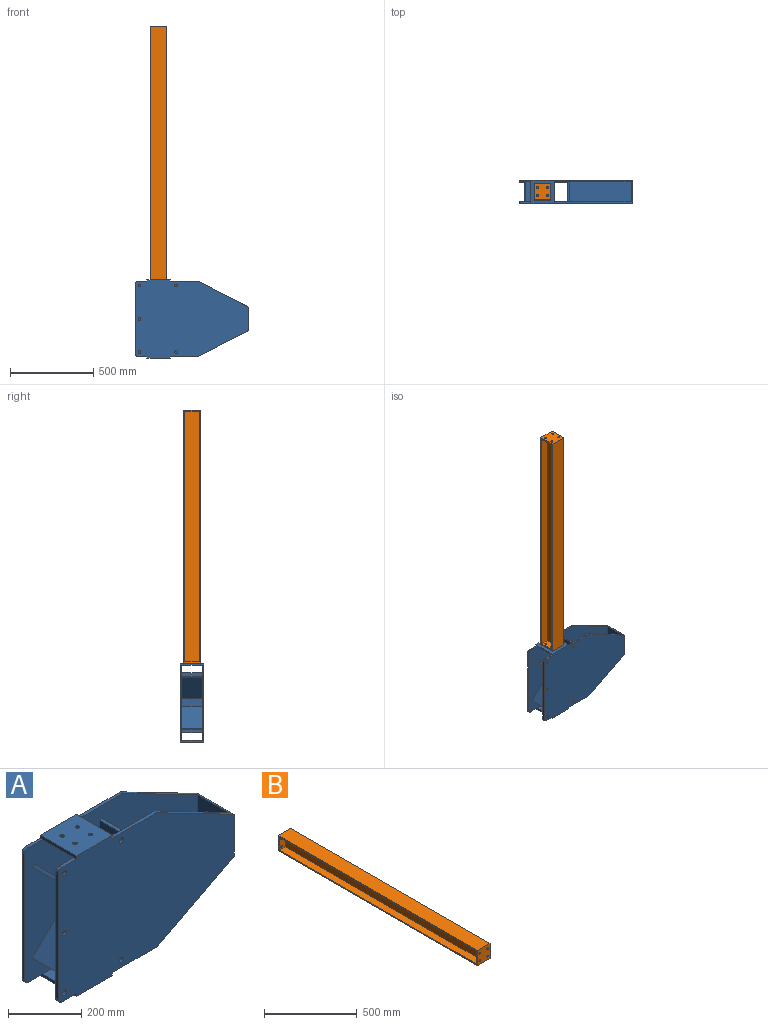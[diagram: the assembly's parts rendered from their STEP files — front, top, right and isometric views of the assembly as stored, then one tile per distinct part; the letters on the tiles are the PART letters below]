
ASSEMBLY  parts=2 mates=1
PART A: 63 faces, bbox 680x140x470 mm
  f0: plane 140x140mm, normal (1,0,0), area 19008.5mm2, adj f11,f12,f19,f41,f59,f60,f61,f62
  f1: plane 120x70.17mm, normal (-1,0,0), area 8124.2mm2, adj f12,f20,f30,f42,f61,f62
  f2: plane 120x70.17mm, normal (-1,0,0), area 8124.2mm2, adj f11,f20,f31,f42,f59,f60
  f3: plane 55x10mm, normal (0,0,-1), area 550mm2, adj f9,f19,f20,f52
  f4: plane 55x10mm, normal (0,0,-1), area 550mm2, adj f40,f41,f42,f52
  f5: plane 55x10mm, normal (0,0,1), area 550mm2, adj f7,f19,f20,f43
  f6: plane 55x10mm, normal (0,0,1), area 550mm2, adj f37,f41,f42,f43
  f7: cylinder r=15mm len=15mm, axis (0,1,0), area 235.6mm2, adj f5,f8,f19,f20
  f8: plane 420x10mm, normal (-1,0,0), area 4200mm2, adj f7,f9,f19,f20
  f9: cylinder r=15mm len=15mm, axis (0,1,0), area 235.6mm2, adj f3,f8,f19,f20
  f10: plane 170x10mm, normal (0,0,-1), area 1700mm2, adj f11,f19,f20,f56
  f11: plane 300x155mm, normal (0.46,0,-0.89), area 8104.2mm2, adj f0,f2,f10,f19,f20,f39,f41,f42
  f12: plane 300x155mm, normal (0.46,0,0.89), area 8104.2mm2, adj f0,f1,f18,f19,f20,f38,f41,f42
  f13: cylinder r=8.5mm len=17mm, axis (0,1,0), area 534.1mm2, adj f19,f20
  f14: cylinder r=8.5mm len=17mm, axis (0,1,0), area 534.1mm2, adj f19,f20
  f15: cylinder r=8.5mm len=17mm, axis (0,1,0), area 534.1mm2, adj f19,f20
  f16: cylinder r=8.5mm len=17mm, axis (0,1,0), area 534.1mm2, adj f19,f20
  f17: cylinder r=8.5mm len=17mm, axis (0,1,0), area 534.1mm2, adj f19,f20
  f18: plane 170x10mm, normal (0,0,1), area 1700mm2, adj f12,f19,f20,f44
  f19: plane 680x470mm, normal (0,-1,0), area 261068.5mm2, adj f0,f3,f5,f7,f8,f9,f10,f11
  f20: plane 670x450mm, normal (0,1,0), area 245916.9mm2, adj f1,f2,f3,f5,f7,f8,f9,f10
  f21: plane 127.28x127.28mm, normal (0.71,0,0.71), area 21600mm2, adj f20,f22,f24,f42
  f22: plane 120x7.07mm, normal (0.71,0,-0.71), area 1200mm2, adj f20,f21,f23,f42
  f23: plane 127.28x127.28mm, normal (-0.71,0,-0.71), area 21600mm2, adj f20,f22,f24,f42
  f24: plane 120x7.07mm, normal (-0.71,0,0.71), area 1200mm2, adj f20,f21,f23,f42
  f25: plane 127.28x127.28mm, normal (-0.71,0,0.71), area 21600mm2, adj f20,f26,f28,f42
  f26: plane 120x7.07mm, normal (0.71,0,0.71), area 1200mm2, adj f20,f25,f27,f42
  f27: plane 127.28x127.28mm, normal (0.71,0,-0.71), area 21600mm2, adj f20,f26,f28,f42
  f28: plane 120x7.07mm, normal (-0.71,0,-0.71), area 1200mm2, adj f20,f25,f27,f42
  f29: plane 175x120mm, normal (1,0,0), area 21000mm2, adj f20,f30,f35,f42
  f30: plane 370x120mm, normal (0,0,1), area 44400mm2, adj f1,f20,f29,f42
  f31: plane 370x120mm, normal (0,0,-1), area 44400mm2, adj f2,f20,f32,f42
  f32: plane 175x120mm, normal (1,0,0), area 21000mm2, adj f20,f31,f33,f42
  f33: plane 120x10mm, normal (0,0,-1), area 1200mm2, adj f20,f32,f34,f42
  f34: plane 360x120mm, normal (-1,0,0), area 43200mm2, adj f20,f33,f35,f42
  f35: plane 120x10mm, normal (0,0,1), area 1200mm2, adj f20,f29,f34,f42
  f36: plane 420x10mm, normal (-1,0,0), area 4200mm2, adj f37,f40,f41,f42
  f37: cylinder r=15mm len=15mm, axis (0,-1,0), area 235.6mm2, adj f6,f36,f41,f42
  f38: plane 170x10mm, normal (0,0,1), area 1700mm2, adj f12,f41,f42,f44
  f39: plane 170x10mm, normal (0,0,-1), area 1700mm2, adj f11,f41,f42,f56
  f40: cylinder r=15mm len=15mm, axis (0,-1,0), area 235.6mm2, adj f4,f36,f41,f42
  f41: plane 680x470mm, normal (0,1,0), area 262203.4mm2, adj f0,f4,f6,f11,f12,f36,f37,f38
  f42: plane 670x450mm, normal (0,-1,0), area 247051.8mm2, adj f1,f2,f4,f6,f11,f12,f21,f22
  f43: plane 140x10mm, normal (-1,0,0), area 1400mm2, adj f5,f6,f19,f41,f49,f50
  f44: plane 140x10mm, normal (1,0,0), area 1400mm2, adj f18,f19,f38,f41,f49,f50
  f45: cylinder r=6mm len=12mm, axis (0,0,-1), area 377mm2, adj f49,f50
  f46: cylinder r=6mm len=12mm, axis (0,0,-1), area 377mm2, adj f49,f50
  f47: cylinder r=6mm len=12mm, axis (0,0,-1), area 377mm2, adj f49,f50
  f48: cylinder r=6mm len=12mm, axis (0,0,-1), area 377mm2, adj f49,f50
  f49: plane 140x140mm, normal (0,0,1), area 19147.6mm2, adj f19,f41,f43,f44,f45,f46,f47,f48
  f50: plane 140x120mm, normal (0,0,-1), area 16347.6mm2, adj f20,f42,f43,f44,f45,f46,f47,f48
  f51: plane 140x120mm, normal (0,0,1), area 16347.6mm2, adj f20,f42,f52,f53,f54,f55,f56,f57
  f52: plane 140x10mm, normal (-1,0,0), area 1400mm2, adj f3,f4,f19,f41,f51,f58
  f53: cylinder r=6mm len=12mm, axis (0,0,1), area 377mm2, adj f51,f58
  f54: cylinder r=6mm len=12mm, axis (0,0,1), area 377mm2, adj f51,f58
  f55: cylinder r=6mm len=12mm, axis (0,0,1), area 377mm2, adj f51,f58
  f56: plane 140x10mm, normal (1,0,0), area 1400mm2, adj f10,f19,f39,f41,f51,f58
  f57: cylinder r=6mm len=12mm, axis (0,0,1), area 377mm2, adj f51,f58
  f58: plane 140x140mm, normal (0,0,-1), area 19147.6mm2, adj f19,f41,f52,f53,f54,f55,f56,f57
  f59: cylinder r=6.86mm len=13.72mm, axis (1,0,0), area 431.1mm2, adj f0,f2
  f60: cylinder r=6.86mm len=13.72mm, axis (1,0,0), area 431.1mm2, adj f0,f2
  f61: cylinder r=6.86mm len=13.72mm, axis (1,0,0), area 431.1mm2, adj f0,f1
  f62: cylinder r=6.86mm len=13.72mm, axis (1,0,0), area 431.1mm2, adj f0,f1
PART B: 24 faces, bbox 96x1520x100 mm
  f0: plane 1500x45.5mm, normal (0,0,-1), area 68250mm2, adj f1,f3,f10,f18
  f1: plane 1500x84mm, normal (-1,0,0), area 126000mm2, adj f0,f2,f10,f18
  f2: plane 1500x45.5mm, normal (0,0,1), area 68250mm2, adj f1,f3,f10,f18
  f3: plane 1520x100mm, normal (-1,0,0), area 26000mm2, adj f0,f2,f4,f9,f10,f16,f18,f23
  f4: plane 1520x96mm, normal (0,0,-1), area 145920mm2, adj f3,f8,f16,f23
  f5: plane 1500x45.5mm, normal (0,0,1), area 68250mm2, adj f6,f8,f11,f17
  f6: plane 1500x84mm, normal (1,0,0), area 126000mm2, adj f5,f7,f11,f17
  f7: plane 1500x45.5mm, normal (0,0,-1), area 68250mm2, adj f6,f8,f11,f17
  f8: plane 1520x100mm, normal (1,0,0), area 26000mm2, adj f4,f5,f7,f9,f11,f16,f17,f23
  f9: plane 1520x96mm, normal (0,0,1), area 145920mm2, adj f3,f8,f16,f23
  f10: plane 84x45.5mm, normal (0,1,0), area 3595.8mm2, adj f0,f1,f2,f3,f12,f15
  f11: plane 84x45.5mm, normal (0,1,0), area 3595.8mm2, adj f5,f6,f7,f8,f13,f14
  f12: cylinder r=6mm len=12mm, axis (0,1,0), area 377mm2, adj f10,f16
  f13: cylinder r=6mm len=12mm, axis (0,1,0), area 377mm2, adj f11,f16
  f14: cylinder r=6mm len=12mm, axis (0,1,0), area 377mm2, adj f11,f16
  f15: cylinder r=6mm len=12mm, axis (0,1,0), area 377mm2, adj f10,f16
  f16: plane 100x96mm, normal (0,-1,0), area 9147.6mm2, adj f3,f4,f8,f9,f12,f13,f14,f15
  f17: plane 84x45.5mm, normal (0,-1,0), area 3595.8mm2, adj f5,f6,f7,f8,f19,f22
  f18: plane 84x45.5mm, normal (0,-1,0), area 3595.8mm2, adj f0,f1,f2,f3,f20,f21
  f19: cylinder r=6mm len=12mm, axis (0,-1,0), area 377mm2, adj f17,f23
  f20: cylinder r=6mm len=12mm, axis (0,-1,0), area 377mm2, adj f18,f23
  f21: cylinder r=6mm len=12mm, axis (0,-1,0), area 377mm2, adj f18,f23
  f22: cylinder r=6mm len=12mm, axis (0,-1,0), area 377mm2, adj f17,f23
  f23: plane 100x96mm, normal (0,1,0), area 9147.6mm2, adj f3,f4,f8,f9,f19,f20,f21,f22
PLACE A t=(95.31,26.75,-82.32)mm
PLACE B rot(axis=(1,0,0),90deg) t=(45.31,86.75,1662.68)mm
MATE slider B.f12 <-> A.f57  axis (0,0,-1) through (15.31,61.75,152.68)mm
